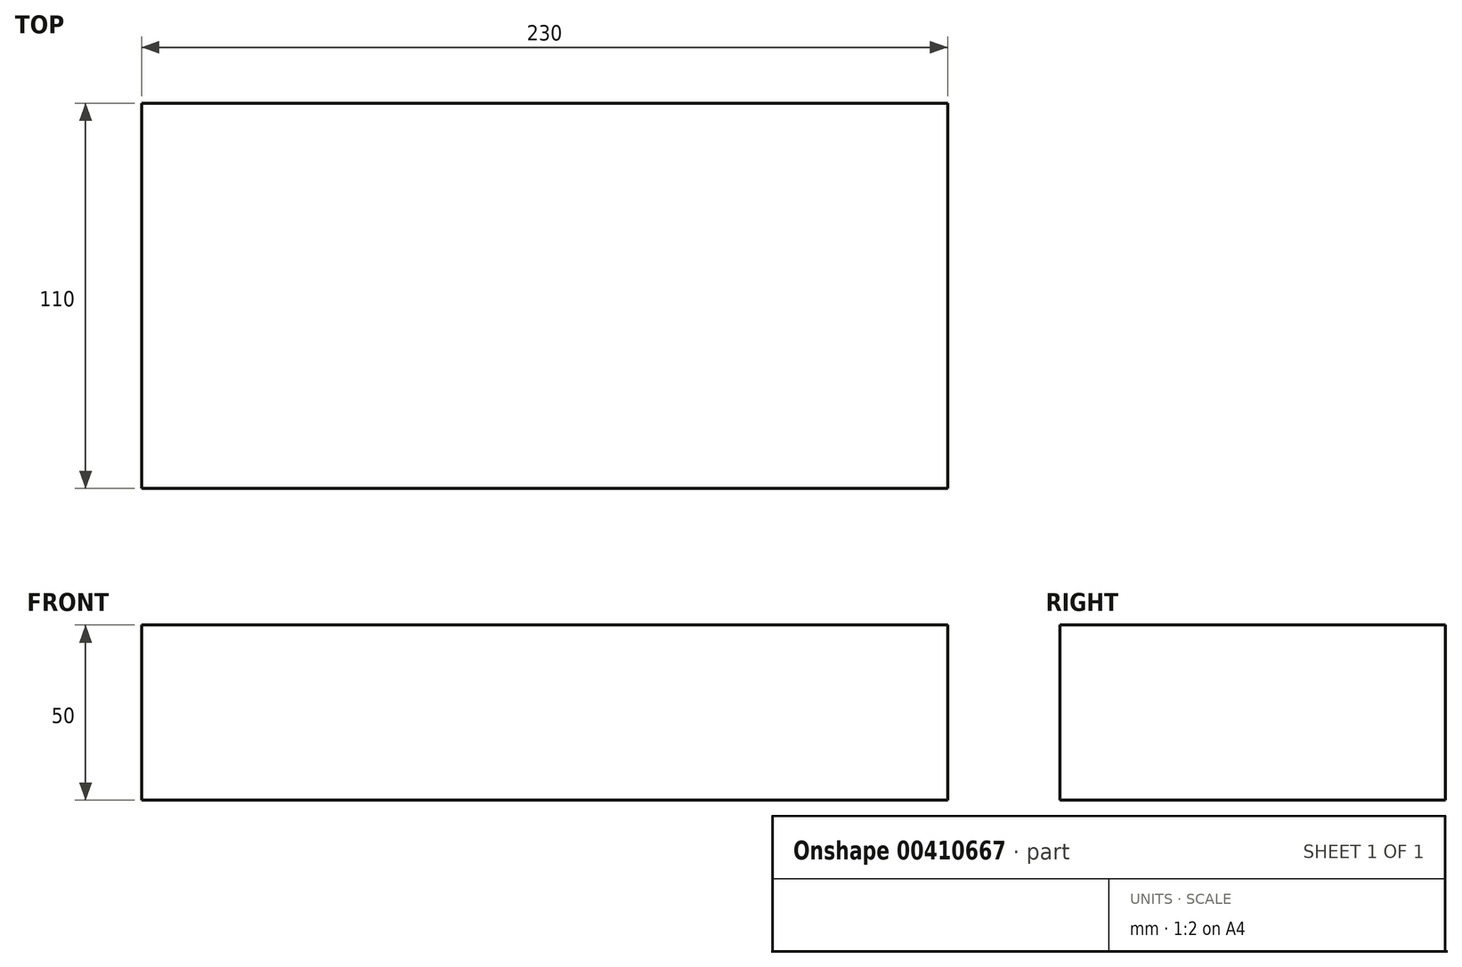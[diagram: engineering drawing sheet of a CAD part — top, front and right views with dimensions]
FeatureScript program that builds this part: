
annotation { "Feature Type Name" : "Feature", "Feature Type Description" : "" }
export const myFeature = defineFeature(function(context is Context, id is Id, definition is map)
    precondition{}
    {
        {
            var Q0;
            Q0=qCreatedBy(makeId("Front.planeOp"),FACE);
            var sketch = newSketch(context, id + "F0", { "sketchPlane" : qUnion([Q0])});
            skLineSegment(sketch, "E0.bottom", {"start": v(115, 25) * mm, "end": v(-115, 25) * mm});
            skLineSegment(sketch, "E0.top", {"start": v(115, -25) * mm, "end": v(-115, -25) * mm});
            skLineSegment(sketch, "E0.left", {"start": v(115, 25) * mm, "end": v(115, -25) * mm});
            skLineSegment(sketch, "E0.right", {"start": v(-115, 25) * mm, "end": v(-115, -25) * mm});
            skPoint(sketch, "E0.middle", {"position": v(0, 0) * mm});
            skSolve(sketch);
        }
        {
            var Q0;
            Q0 = qSketchRegion(id + "F0", true);
            extrude(context, id + "F1", {"entities" : qUnion([Q0]), "endBound" : BoundingType.SYMMETRIC, "depth" : 110 * mm});
        }
    });
